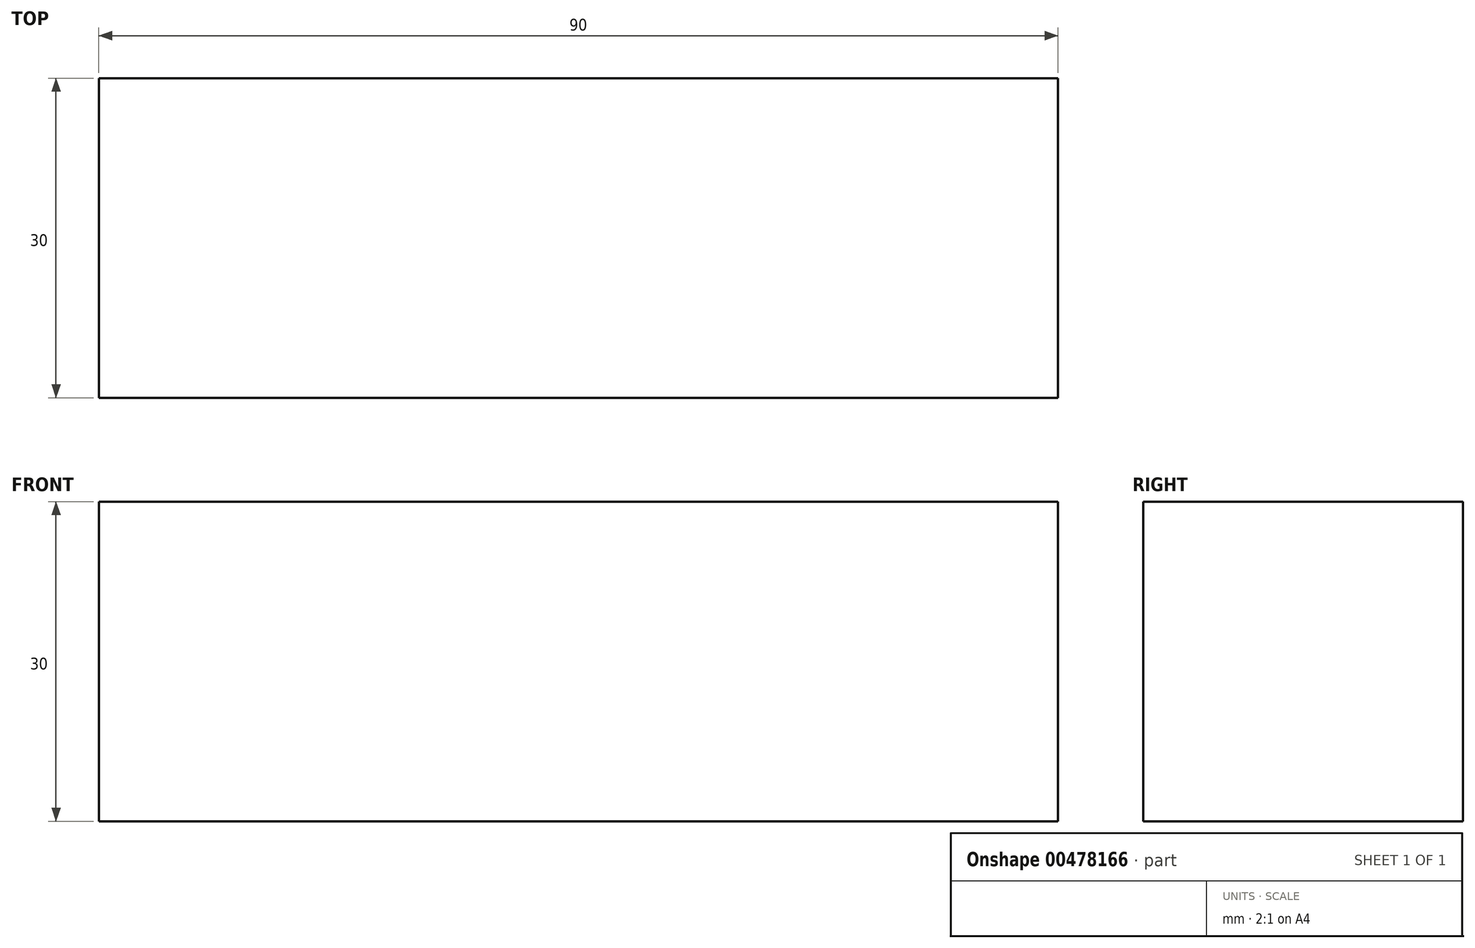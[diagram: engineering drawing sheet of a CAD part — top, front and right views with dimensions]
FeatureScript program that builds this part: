
annotation { "Feature Type Name" : "Feature", "Feature Type Description" : "" }
export const myFeature = defineFeature(function(context is Context, id is Id, definition is map)
    precondition{}
    {
        {
            var Q0;
            Q0=qCreatedBy(makeId("Top.planeOp"),FACE);
            var sketch = newSketch(context, id + "F0", { "sketchPlane" : qUnion([Q0])});
            skLineSegment(sketch, "E0.bottom", {"start": v(-45.45, -3.06) * mm, "end": v(44.55, -3.06) * mm});
            skLineSegment(sketch, "E0.top", {"start": v(-45.45, -33.06) * mm, "end": v(44.55, -33.06) * mm});
            skLineSegment(sketch, "E0.left", {"start": v(-45.45, -3.06) * mm, "end": v(-45.45, -33.06) * mm});
            skLineSegment(sketch, "E0.right", {"start": v(44.55, -3.06) * mm, "end": v(44.55, -33.06) * mm});
            skSolve(sketch);
        }
        {
            var Q0;
            Q0=makeQuery(id+"F0.imprint","IMPRINT",FACE,{"disambiguationData":[TD([[makeQuery(id+"F0.imprint","IMPRINT",EDGE,{"derivedFrom":sQuery(id+"F0.wireOp",EDGE,"E0.bottom")}),-1.0]])]});
            extrude(context, id + "F1", {"entities" : qUnion([Q0]), "depth" : 30 * mm});
        }
    });
